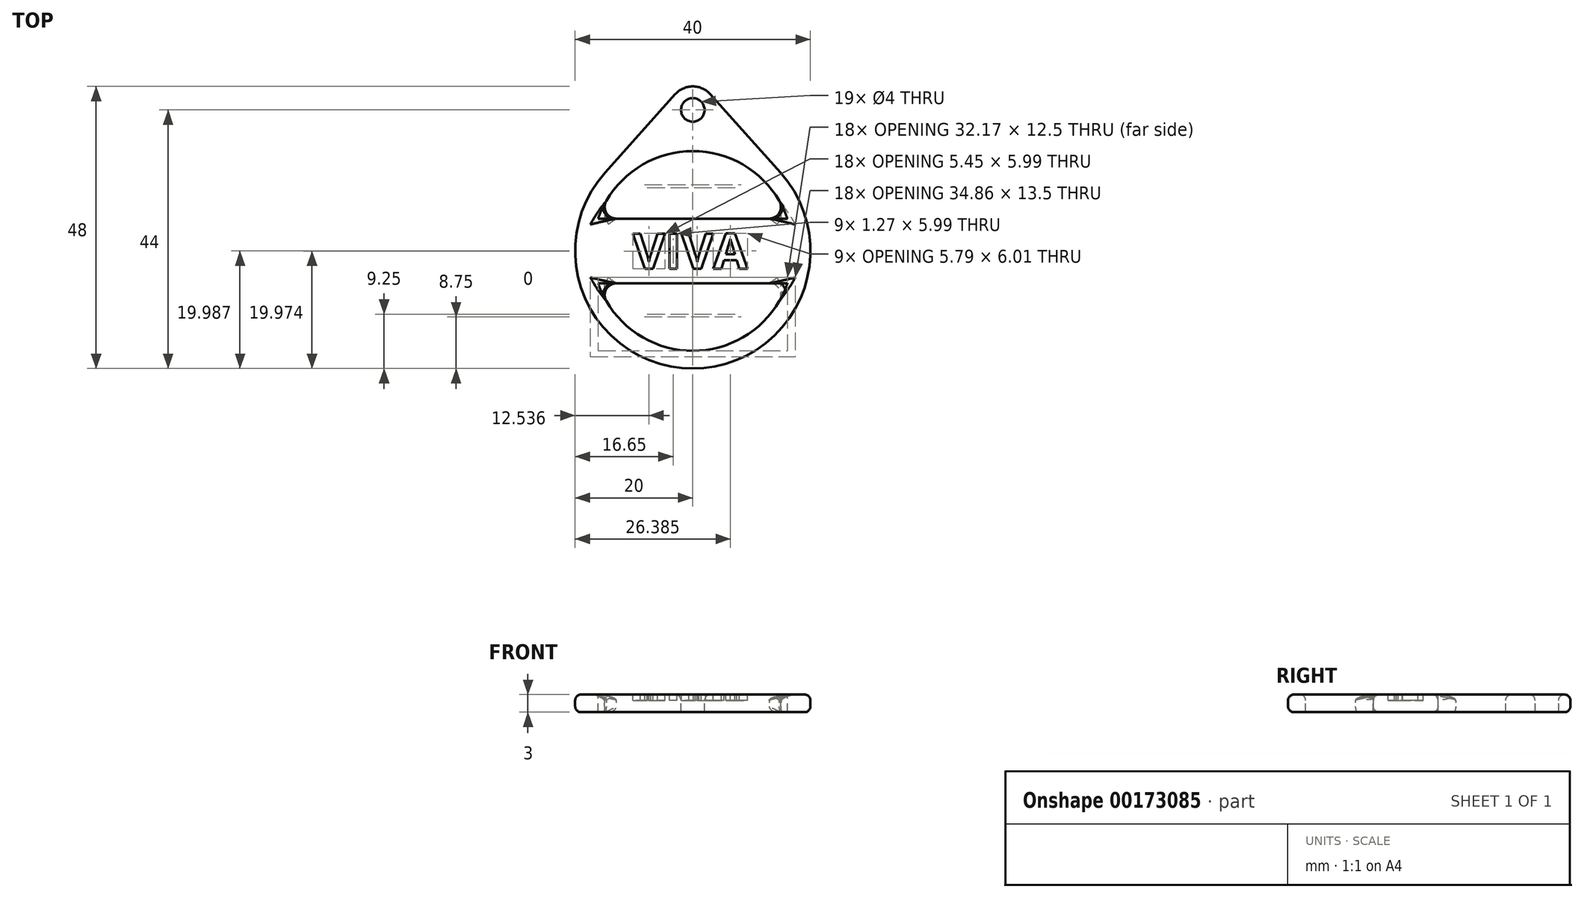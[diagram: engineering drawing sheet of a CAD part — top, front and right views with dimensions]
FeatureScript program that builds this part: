
annotation { "Feature Type Name" : "Feature", "Feature Type Description" : "" }
export const myFeature = defineFeature(function(context is Context, id is Id, definition is map)
    precondition{}
    {
        {
            var Q0;
            Q0=qCreatedBy(makeId("Top.planeOp"),FACE);
            var sketch = newSketch(context, id + "F0", { "sketchPlane" : qUnion([Q0])});
            skCircle(sketch, "E0", {"center": v(0, 0) * mm, "radius": 20 * mm});
            skCircle(sketch, "E1", {"center": v(0, 24) * mm, "radius": 4 * mm});
            skPoint(sketch, "E2", {"position": v(0, 20) * mm});
            skLineSegment(sketch, "E3", {"start": v(2.98, 26.67) * mm, "end": v(14.9, 13.33) * mm});
            skLineSegment(sketch, "E4", {"start": v(-2.98, 26.67) * mm, "end": v(-14.9, 13.33) * mm});
            skSolve(sketch);
        }
        {
            var Q0;
            Q0 = qSketchRegion(id + "F0", true);
            extrude(context, id + "F1", {"entities" : qUnion([Q0]), "depth" : 3 * mm});
        }
        {
            var Q0;
            Q0=makeQuery(id+"F1.opExtrude","CAP_FACE",FACE,{"disambiguationData":[OSD([sQuery(id+"F0.wireOp",EDGE,"E0"),sQuery(id+"F0.wireOp",EDGE,"E1"),sQuery(id+"F0.wireOp",EDGE,"E3"),sQuery(id+"F0.wireOp",EDGE,"E4")])],"isStart":false});
            var sketch = newSketch(context, id + "F2", { "sketchPlane" : qUnion([Q0])});
            skCircle(sketch, "E5", {"center": v(0, 24) * mm, "radius": 2.5 * mm});
            skSolve(sketch);
        }
        {
            var Q0;
            Q0=sQuery(id+"F2.wireOp",VERTEX,"E5.center");
            var Q1;
            Q1=makeQuery(id+"F1.opExtrude","SWEPT_BODY",BODY,{"disambiguationData":[OSD([sQuery(id+"F0.wireOp",EDGE,"E0"),sQuery(id+"F0.wireOp",EDGE,"E1"),sQuery(id+"F0.wireOp",EDGE,"E3"),sQuery(id+"F0.wireOp",EDGE,"E4")])]});
            hole(context, id + "F3", {"style" : HoleStyle.SIMPLE, "endStyle" : HoleEndStyle.THROUGH, "holeDiameter" : 4 * mm, "locations" : qUnion([Q0]), "scope" : qUnion([Q1]), "isTappedThrough" : true});
        }
        {
            var Q0;
            Q0=makeQuery(id+"F1.opExtrude","CAP_FACE",FACE,{"disambiguationData":[OSD([sQuery(id+"F0.wireOp",EDGE,"E0"),sQuery(id+"F0.wireOp",EDGE,"E1"),sQuery(id+"F0.wireOp",EDGE,"E3"),sQuery(id+"F0.wireOp",EDGE,"E4")])],"isStart":false});
            var sketch = newSketch(context, id + "F4", { "sketchPlane" : qUnion([Q0])});
            skArc(sketch, "E6", {"start": v(-16.09, -5.5) * mm, "mid": v(0, -17) * mm, "end": v(16.09, -5.5) * mm});
            skLineSegment(sketch, "E7.bottom", {"start": v(16.09, 5.5) * mm, "end": v(-16.09, 5.5) * mm});
            skLineSegment(sketch, "E7.top", {"start": v(16.09, -5.5) * mm, "end": v(-16.09, -5.5) * mm});
            skPoint(sketch, "E8.orphan", {"position": v(-17.62, 5.5) * mm});
            skPoint(sketch, "E9.orphan", {"position": v(-17.62, -5.5) * mm});
            skPoint(sketch, "E7.left.start.orphan", {"position": v(17.62, 5.5) * mm});
            skArc(sketch, "E10.trimOffspring", {"start": v(16.09, 5.5) * mm, "mid": v(0, 17) * mm, "end": v(-16.09, 5.5) * mm});
            skPoint(sketch, "E11.orphan", {"position": v(17.62, -5.5) * mm});
            skSolve(sketch);
        }
        {
            var Q0;
            Q0 = qSketchRegion(id + "F4", true);
            extrude(context, id + "F5", {"entities" : qUnion([Q0]), "operationType" : NewBodyOperationType.REMOVE, "oppositeDirection" : true, "depth" : 25 * mm});
        }
        {
            var Q0;
            Q0=makeQuery(id+"F1.opExtrude","CAP_EDGE",EDGE,{"disambiguationData":[OSD([sQuery(id+"F0.wireOp",EDGE,"E0")])],"isStart":false});
            var Q1;
            Q1=makeQuery(id+"F1.opExtrude","CAP_EDGE",EDGE,{"disambiguationData":[OSD([sQuery(id+"F0.wireOp",EDGE,"E0")])],"isStart":true});
            var Q2;
            Q2=makeQuery(id+"F3.hole-0.boolean.opBoolean","COPY",EDGE,{"derivedFrom":makeQuery(id+"F3.hole-0.opRevolve","SWEPT_EDGE",EDGE,{"disambiguationData":[OSD([sQuery(id+"F3.hole-0.sketch.wireOp",EDGE,"core_line_2"),sQuery(id+"F3.hole-0.sketch.wireOp",EDGE,"core_line_3")])]})});
            var Q3;
            Q3=makeQuery(id+"F1.opExtrude","CAP_FACE",FACE,{"disambiguationData":[OSD([sQuery(id+"F0.wireOp",EDGE,"E0"),sQuery(id+"F0.wireOp",EDGE,"E1"),sQuery(id+"F0.wireOp",EDGE,"E3"),sQuery(id+"F0.wireOp",EDGE,"E4")])],"isStart":false});
            var Q4;
            Q4=makeQuery(id+"F3.hole-0.boolean.opBoolean","INTERSECT",EDGE,{"derivedFrom":[makeQuery(id+"F1.opExtrude","CAP_FACE",FACE,{"disambiguationData":[OSD([sQuery(id+"F0.wireOp",EDGE,"E0"),sQuery(id+"F0.wireOp",EDGE,"E1"),sQuery(id+"F0.wireOp",EDGE,"E3"),sQuery(id+"F0.wireOp",EDGE,"E4")])],"isStart":true}),makeQuery(id+"F3.hole-0.opRevolve","SWEPT_FACE",FACE,{"disambiguationData":[OSD([sQuery(id+"F3.hole-0.sketch.wireOp",EDGE,"core_line_2")])]})]});
            var Q5;
            Q5=makeQuery(id+"F5.boolean.opBoolean","INTERSECT",EDGE,{"derivedFrom":[makeQuery(id+"F1.opExtrude","CAP_FACE",FACE,{"disambiguationData":[OSD([sQuery(id+"F0.wireOp",EDGE,"E0"),sQuery(id+"F0.wireOp",EDGE,"E1"),sQuery(id+"F0.wireOp",EDGE,"E3"),sQuery(id+"F0.wireOp",EDGE,"E4")])],"isStart":true}),makeQuery(id+"F5.opExtrude","SWEPT_FACE",FACE,{"disambiguationData":[OSD([sQuery(id+"F4.wireOp",EDGE,"E7.bottom")])]})]});
            var Q6;
            Q6=makeQuery(id+"F5.boolean.opBoolean","INTERSECT",EDGE,{"derivedFrom":[makeQuery(id+"F1.opExtrude","CAP_FACE",FACE,{"disambiguationData":[OSD([sQuery(id+"F0.wireOp",EDGE,"E0"),sQuery(id+"F0.wireOp",EDGE,"E1"),sQuery(id+"F0.wireOp",EDGE,"E3"),sQuery(id+"F0.wireOp",EDGE,"E4")])],"isStart":true}),makeQuery(id+"F5.opExtrude","SWEPT_FACE",FACE,{"disambiguationData":[OSD([sQuery(id+"F4.wireOp",EDGE,"E7.top")])]})]});
            fillet(context, id + "F6", {"entities" : qUnion([Q0, Q1, Q2, Q3, Q4, Q5, Q6]), "radius" : 1 * mm, "tangentPropagation" : true, "allowEdgeOverflow" : false});
        }
        {
            var Q0;
            {var subQ0=sQuery(id+"F4.wireOp",EDGE,"E10.trimOffspring");var subQ1=sQuery(id+"F4.wireOp",EDGE,"E7.bottom");Q0=makeQuery(id+"F5.boolean.opBoolean","COPY",EDGE,{"derivedFrom":makeQuery(id+"F5.opExtrude","SWEPT_EDGE",EDGE,{"disambiguationData":[OSD([subQ1,subQ0]),TDD([makeQuery(id+"F4.imprint","INTERSECT",VERTEX,{"disambiguationData":[OD(1.0)],"derivedFrom":[subQ1,subQ0]})])]})});}
            var Q1;
            {var subQ0=sQuery(id+"F4.wireOp",EDGE,"E10.trimOffspring");var subQ1=sQuery(id+"F4.wireOp",EDGE,"E7.bottom");Q1=makeQuery(id+"F5.boolean.opBoolean","COPY",EDGE,{"derivedFrom":makeQuery(id+"F5.opExtrude","SWEPT_EDGE",EDGE,{"disambiguationData":[OSD([subQ1,subQ0]),TDD([makeQuery(id+"F4.imprint","INTERSECT",VERTEX,{"disambiguationData":[OD(0.0)],"derivedFrom":[subQ1,subQ0]})])]})});}
            var Q2;
            {var subQ0=sQuery(id+"F4.wireOp",EDGE,"E7.top");var subQ1=sQuery(id+"F4.wireOp",EDGE,"E6");Q2=makeQuery(id+"F5.boolean.opBoolean","COPY",EDGE,{"derivedFrom":makeQuery(id+"F5.opExtrude","SWEPT_EDGE",EDGE,{"disambiguationData":[OSD([subQ1,subQ0]),TDD([makeQuery(id+"F4.imprint","INTERSECT",VERTEX,{"disambiguationData":[OD(0.0)],"derivedFrom":[subQ1,subQ0]})])]})});}
            var Q3;
            {var subQ0=sQuery(id+"F4.wireOp",EDGE,"E7.top");var subQ1=sQuery(id+"F4.wireOp",EDGE,"E6");Q3=makeQuery(id+"F5.boolean.opBoolean","COPY",EDGE,{"derivedFrom":makeQuery(id+"F5.opExtrude","SWEPT_EDGE",EDGE,{"disambiguationData":[OSD([subQ1,subQ0]),TDD([makeQuery(id+"F4.imprint","INTERSECT",VERTEX,{"disambiguationData":[OD(1.0)],"derivedFrom":[subQ1,subQ0]})])]})});}
            fillet(context, id + "F7", {"entities" : qUnion([Q0, Q1, Q2, Q3]), "radius" : 2 * mm, "tangentPropagation" : true, "allowEdgeOverflow" : false});
        }
        {
            var Q0;
            Q0=makeQuery(id+"F1.opExtrude","CAP_FACE",FACE,{"disambiguationData":[OSD([sQuery(id+"F0.wireOp",EDGE,"E0"),sQuery(id+"F0.wireOp",EDGE,"E1"),sQuery(id+"F0.wireOp",EDGE,"E3"),sQuery(id+"F0.wireOp",EDGE,"E4")])],"isStart":false});
            var sketch = newSketch(context, id + "F8", { "sketchPlane" : qUnion([Q0])});
            skPoint(sketch, "E12", {"position": v(4.77, -1.57) * mm});
            skText(sketch, "E13", { "text": "VIVA", "fontName": "OpenSans-Bold.ttf"});
            const initialGuessF8  = {"E13": [-0.01019, -0.00302, 1, 0, 0.00604]};
            skSetInitialGuess(sketch, initialGuessF8);
            skSolve(sketch);
        }
        {
            var Q0;
            Q0 = qSketchRegion(id + "F8", true);
            extrude(context, id + "F9", {"entities" : qUnion([Q0]), "operationType" : NewBodyOperationType.REMOVE, "oppositeDirection" : true, "depth" : 1 * mm});
        }
    });
